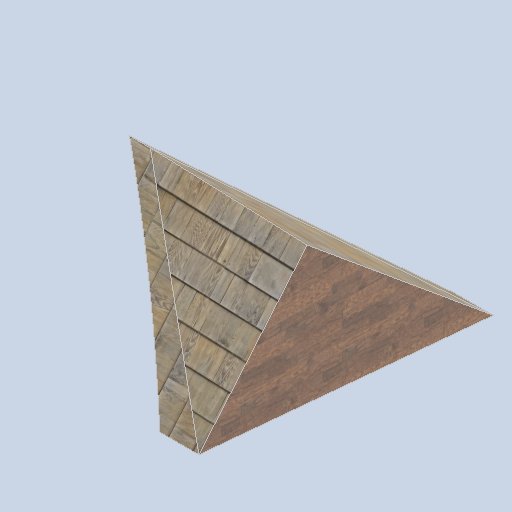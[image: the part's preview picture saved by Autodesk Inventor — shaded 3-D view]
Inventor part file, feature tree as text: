
AUTODESK INVENTOR PART (.ipt)
format: ipt  version: 2024.2 (Build 282272000, 272)  size: 242,176 bytes
history: native  units: in
note: dims shown in document units (in); Inventor stores cm internally (conversion verified against a paired STEP export)
features: sketch x6, plane x5, other x3
ambient origin geometry x8: Origin, YZ Plane, XZ Plane, XY Plane, X Axis, Y Axis, Z Axis, Center Point
bodies: Solid1 (feature_tree)
feature tree (14):
  other  "panel_pad_03.ipt"
  other  "Solid1::panel_pad_03.ipt"
  other  "TaggingFeature1"
  sketch  "Sketch1"  dims[d0=0.3937in]
  sketch  "Sketch2"
  sketch  "Sketch3"
  sketch  "Sketch6"
  sketch  "Sketch7"
  sketch  "Sketch8"
  plane  "Work Plane1"
  plane  "Work Plane2"
  plane  "Work Plane3"
  plane  "Work Plane4"
  plane  "Work Plane5"
